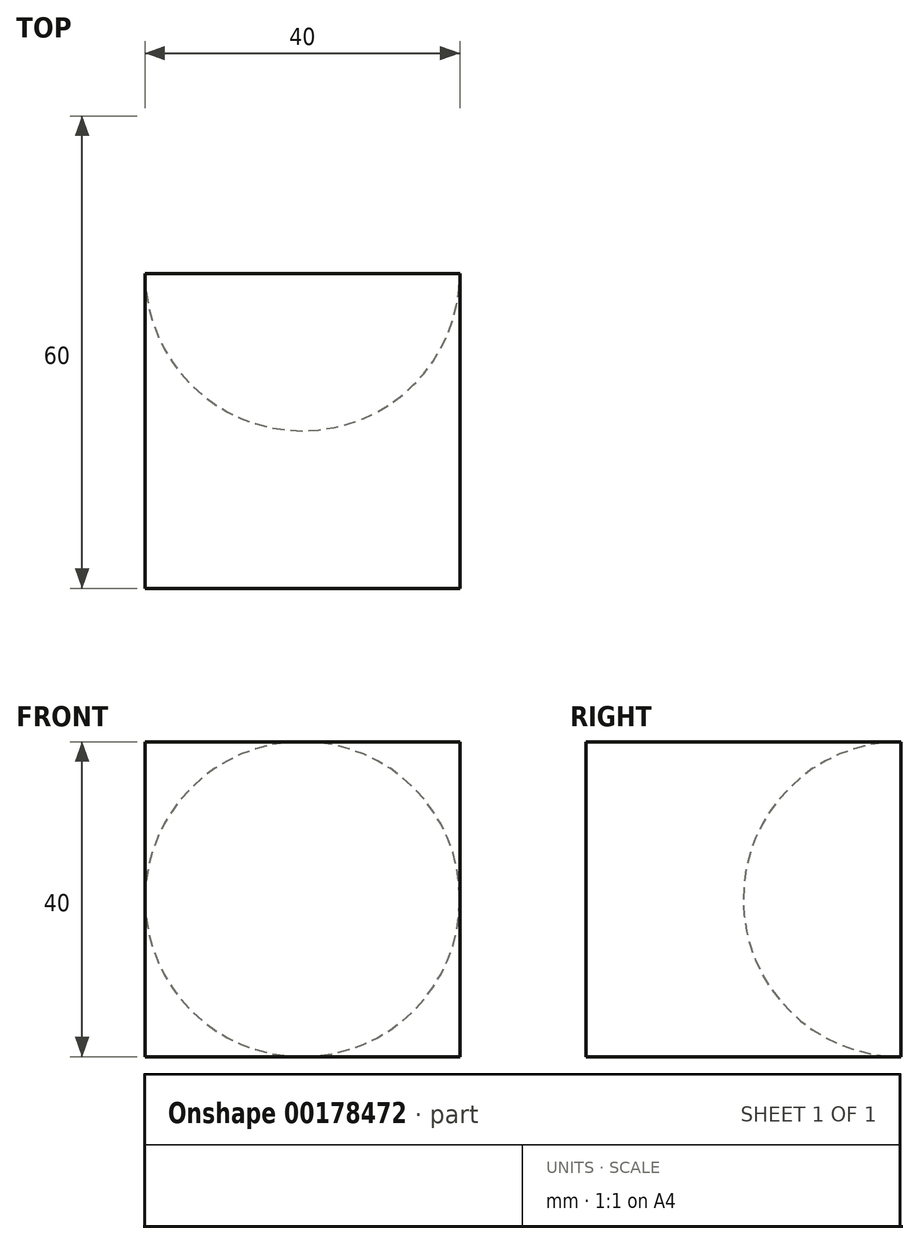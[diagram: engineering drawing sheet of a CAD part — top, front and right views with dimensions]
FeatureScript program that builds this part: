
annotation { "Feature Type Name" : "Feature", "Feature Type Description" : "" }
export const myFeature = defineFeature(function(context is Context, id is Id, definition is map)
    precondition{}
    {
        {
            var Q0;
            Q0=qCreatedBy(makeId("Top.planeOp"),FACE);
            var sketch = newSketch(context, id + "F0", { "sketchPlane" : qUnion([Q0])});
            skLineSegment(sketch, "E0.bottom", {"start": v(0, 0) * mm, "end": v(40, 0) * mm});
            skLineSegment(sketch, "E0.top", {"start": v(0, 40) * mm, "end": v(40, 40) * mm});
            skLineSegment(sketch, "E0.left", {"start": v(0, 0) * mm, "end": v(0, 40) * mm});
            skLineSegment(sketch, "E0.right", {"start": v(40, 0) * mm, "end": v(40, 40) * mm});
            skSolve(sketch);
        }
        {
            var Q0;
            Q0 = qSketchRegion(id + "F0", true);
            extrude(context, id + "F1", {"entities" : qUnion([Q0]), "depth" : 40 * mm});
        }
        {
            var Q0;
            Q0=makeQuery(id+"F1.opExtrude","SWEPT_FACE",FACE,{"disambiguationData":[OSD([sQuery(id+"F0.wireOp",EDGE,"E0.top")])]});
            var sketch = newSketch(context, id + "F2", { "sketchPlane" : qUnion([Q0])});
            skLineSegment(sketch, "E1", {"start": v(-20, 0) * mm, "end": v(-20, 40) * mm});
            skPoint(sketch, "E2", {"position": v(-40, 20) * mm});
            skArc(sketch, "E3", {"start": v(-20, 40) * mm, "mid": v(-40, 20) * mm, "end": v(-20, 0) * mm});
            skSolve(sketch);
        }
        {
            var Q0;
            {var subQ0=sQuery(id+"F2.wireOp",EDGE,"E1");Q0=makeQuery(id+"F2.imprint","IMPRINT",FACE,{"disambiguationData":[TD([[makeQuery(id+"F2.imprint","IMPRINT",EDGE,{"derivedFrom":subQ0}),1.0]])]});}
            var Q1;
            Q1=sQuery(id+"F2.wireOp",EDGE,"E1");
            revolve(context, id + "F3", {"operationType" : NewBodyOperationType.REMOVE, "entities" : qUnion([Q0]), "axis" : qUnion([Q1]), "revolveType" : RevolveType.FULL, "oppositeDirection" : true});
        }
    });
